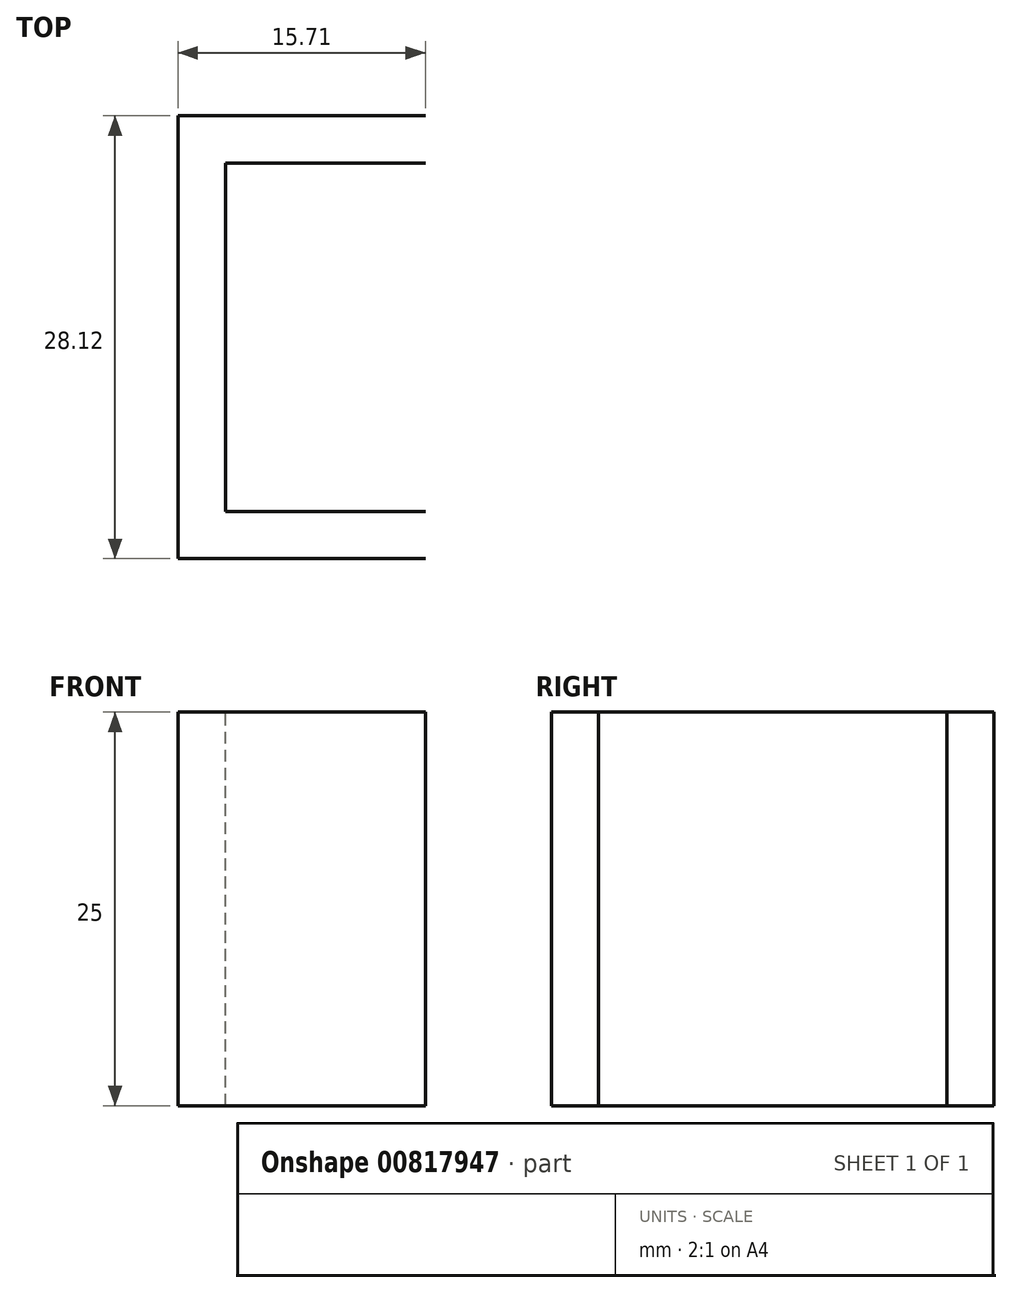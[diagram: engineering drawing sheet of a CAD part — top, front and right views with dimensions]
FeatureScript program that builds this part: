
annotation { "Feature Type Name" : "Feature", "Feature Type Description" : "" }
export const myFeature = defineFeature(function(context is Context, id is Id, definition is map)
    precondition{}
    {
        {
            var Q0;
            Q0=qCreatedBy(makeId("Top.planeOp"),FACE);
            var sketch = newSketch(context, id + "F0", { "sketchPlane" : qUnion([Q0])});
            skLineSegment(sketch, "E0.bottom", {"start": v(-53.44, 47.81) * mm, "end": v(-37.73, 47.81) * mm});
            skLineSegment(sketch, "E0.top", {"start": v(-53.44, 19.69) * mm, "end": v(-37.73, 19.69) * mm});
            skLineSegment(sketch, "E0.left", {"start": v(-53.44, 47.81) * mm, "end": v(-53.44, 19.69) * mm});
            skArc(sketch, "E1", {"start": v(-37.73, 19.69) * mm, "mid": v(-7.47, 33.75) * mm, "end": v(-37.73, 47.81) * mm});
            skArc(sketch, "E2.0", {"start": v(-35.8, 21.98) * mm, "mid": v(-10.47, 33.75) * mm, "end": v(-35.8, 45.52) * mm});
            skLineSegment(sketch, "E3.0", {"start": v(-50.44, 44.81) * mm, "end": v(-37.73, 44.81) * mm});
            skLineSegment(sketch, "E3.1", {"start": v(-50.44, 44.81) * mm, "end": v(-50.44, 22.69) * mm});
            skLineSegment(sketch, "E3.2", {"start": v(-50.44, 22.69) * mm, "end": v(-37.73, 22.69) * mm});
            skLineSegment(sketch, "E4", {"start": v(-37.73, 44.81) * mm, "end": v(-35.8, 45.52) * mm});
            skLineSegment(sketch, "E5", {"start": v(-35.8, 21.98) * mm, "end": v(-37.73, 22.69) * mm});
            skSolve(sketch);
        }
        {
            var Q0;
            Q0=sQuery(id+"F0.wireOp",EDGE,"E3.0");
            var Q1;
            Q1=sQuery(id+"F0.wireOp",EDGE,"E0.top");
            var Q2;
            Q2=sQuery(id+"F0.wireOp",EDGE,"E3.1");
            var Q3;
            Q3=sQuery(id+"F0.wireOp",EDGE,"E3.2");
            var Q4;
            Q4=sQuery(id+"F0.wireOp",EDGE,"E0.left");
            var Q5;
            Q5=sQuery(id+"F0.wireOp",EDGE,"E0.bottom");
            extrude(context, id + "F1", {"bodyType" : ToolBodyType.SURFACE, "surfaceEntities" : qUnion([Q0, Q1, Q2, Q3, Q4, Q5]), "depth" : 25 * mm, "offsetDistance" : 25 * mm});
        }
    });
